# Revit family: L-12
name_source: partatom
category: Lighting Fixtures
revit_build: Autodesk Revit MEP 2012 (Build: 20110916_2132(x64)
units: mm (PartAtom-declared; Revit-internal decimal feet)

## types (2) — shared parameters
Apparent Load = 0 VA
Backbox = White
Default Elevation = 4' - 0"
Description = An extremely versatile fixture family, Knife & Rail provide a wide range of light outputs, luminaire distributions and fixture designs to meet a variety of application needs.
Glass = White Glass
Lamp = LED
Manufacturer = Litecontrol Lighting
Manufacturer Fax = 781-293-2849
Model = L12
Nominal Watts = 37 W
Product Documentation Link = http://www.litecontrol.com
Product Page URL = http://www.litecontrol.com
URL = http://www.litecontrol.com
Voltage = 120 V

## per-type parameters (varying)
| type | Length | Photometric Web |
| L-12-4' | 4' - 0" | Web L12 : p_id_l12_04_sof_lpa_35k_i10_d15 |
| L-12-8' | 8' - 0" | Web L12 : p_id_l12_04_sof_lpa_35k_i10_d35 |

## geometry (parser evidence)
native form markers: Sweep x8
no freeform markers — native parametric forms only
